# Revit family: CU2HL
name_source: partatom
category: Lighting Fixtures
units: mm (PartAtom-declared; Revit-internal decimal feet)

## family parameters
Cut with Voids When Loaded = No
Host = Face
Light Source = No
OmniClass Number = 23.80.70.11.14.17
OmniClass Title = Direct/Indirect
Part Type = Normal
Room Calculation Point = No
Round Connector Dimension = Use Diameter
Shared = Yes

## types (1)
- CU2HL
    Angle Tilt = 60°
    Apparent Load = 3 VA
    Assembly Code = D5020200
    Black = Paint - White Texture
    Connector Description = Lighting Connector
    Default Elevation = 48 "
    Description = The CU2HL Series is a high lumen output emergency light which includes a longlife Lithium Iron Phosphate battery, and adjustable high-power LED lamp heads
    Fixture distribution = Direct
    Glass = Glass
    Height = 2.5 "
    Housing Material = Paint - White Texture
    Lamp = LED
    Length = 24 "
    Load Classification = Lighting
    Manufacturer = Compass Products
    Model = CU2HL
    Mounting = Paint - Light Silver
    Power Factor = 1
    Reflector Finish = White Glass
    URL = https://www.currentlighting.com
    Voltage = 120 V
    Warranty = 5 year Warranty
    Wattage Comments = 3W
    Watts = 3 W
    Width = 12.125 "
    Wings = Paint - Light Silver
    zz Angle = 60°

## geometry (parser evidence)
native form markers: Sweep x5
no freeform markers — native parametric forms only
